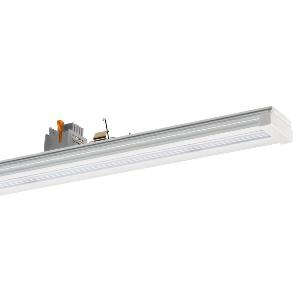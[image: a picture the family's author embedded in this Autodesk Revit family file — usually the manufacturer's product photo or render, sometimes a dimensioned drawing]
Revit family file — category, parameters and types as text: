
# Revit family: conveo_-_cvg_8000_850_xn-p_da_7_226848169-00804954_7ea8
name_source: partatom
category: Lighting Fixtures
units: mm (PartAtom-declared; Revit-internal decimal feet)

## family parameters
Cut with Voids When Loaded = No
Host = Face
Light Source = No
Part Type = Normal
Room Calculation Point = No
Round Connector Dimension = Use Diameter
Shared = No

## types (1)
- CONVEO - CVG 8000/850/xN-P/DA/7 (1 x LED, 7800 lm, 5000K)
    Apparent Load = 55 VA
    Approval mark = CE
    CIE Flux Codes = 57 84 97 100 100
    Color Rendering = 80-89
    Color Temperature = 5000K
    Control Gear = Electronic ballast
    Default Elevation = 1800 mm
    Description = CVG 8000/850/xN-P/DA/7|Continuous-row system|light source: LED|work equipment: Adjustable electronic ballast, digital DALI|connected load: 220-240 V, 50-60 Hz|Power consumption: approx. 55 W|luminous flux: 7800 lm|luminous efficacy: 141 lm/W|colour temperature: Cold white, ca. 5000 K|color rendering index (CRI): >= 80|chromaticity tolerance:  3 SDCM|System of protection: IP 54|class of protection: I|technology: Continuously dimmable|luminaire body|material: Aluminium|surface: Powder coatet|colour: White|lamp cover: Acrylic (PMMA), Satine|weight (net): approx. 1.9 kg|Fastening: Available separately|minimum ambient temperature: -25 ░C|maximum ambient temperature: 45 ░C|glare control: Prism optics (linear)|Approval mark: VDE - ENEC|
    Frequency = 50 Hz
    Height = 70 mm
    Lamp = 1 x LED
    Lamp Light Flux = 7800 lm
    Lamp count = 1
    Length = 1500 mm
    Luminous efficacy = 142 lm/W
    Manufacturer = Waldmann
    ModVariant = No
    Model = 226848169-00804954
    Mounting Place = Ceiling
    Mounting Type = Pendant
    Number of Poles = 1
    OnlyDefault = Yes
    Power Factor = 1
    Product Name = CONVEO - CVG 8000/850/xN-P/DA/7
    Product group = Continuous-row system (industry)
    ProductGroupID = 301
    Protection Class = Protection class I
    Protection Degree = IP 54
    RLX_Detail_Level = 1
    RlxData = <blob elided: 99973 chars, md5=b906787f>
    Socket = socket
    Standby Power = 0 W
    System Light Flux = 7800 lm
    System Power = 55 W
    Type Comments = Product without accessories
    Type Image = 226848019-00804937-1p7.jpg
    URL = http://relux.com
    VarID = ---
    Voltage = 230 V
    Voltage Range = 220-240 V
    Weight = 0.00 kg
    Width = 64 mm

## geometry (parser evidence)
native form markers: Blend x4, Sweep x8
no freeform markers — native parametric forms only
